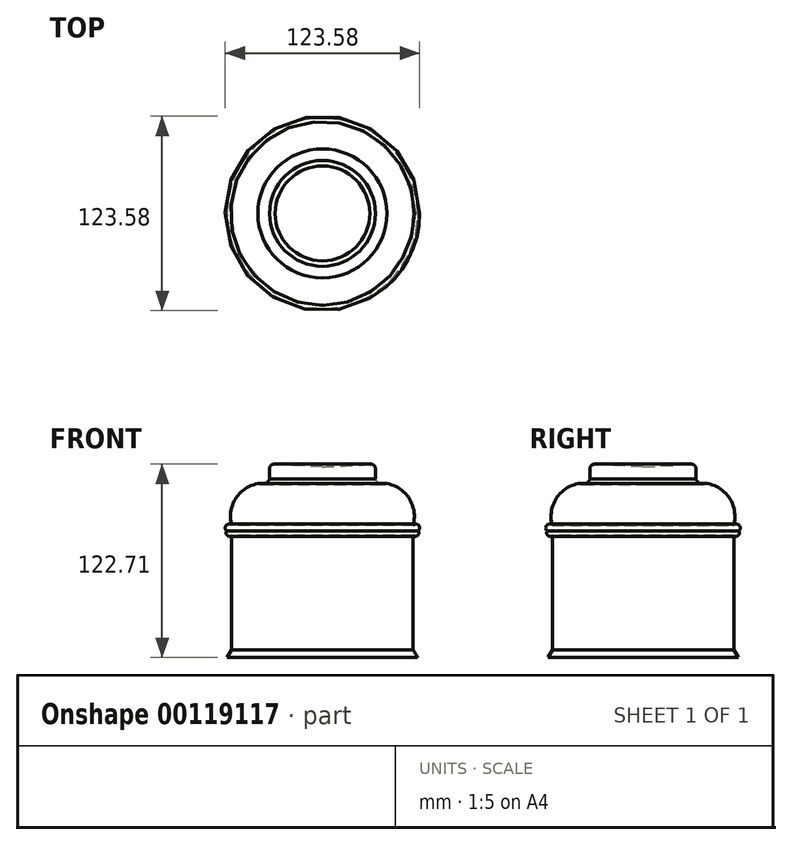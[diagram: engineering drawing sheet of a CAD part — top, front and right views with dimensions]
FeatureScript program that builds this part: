
annotation { "Feature Type Name" : "Feature", "Feature Type Description" : "" }
export const myFeature = defineFeature(function(context is Context, id is Id, definition is map)
    precondition{}
    {
        {
            var Q0;
            Q0=qCreatedBy(makeId("Front.planeOp"),FACE);
            var sketch = newSketch(context, id + "F0", { "sketchPlane" : qUnion([Q0])});
            skLineSegment(sketch, "E0", {"start": v(-30.08, 58.25) * mm, "end": v(-30.08, -62.73) * mm});
            skLineSegment(sketch, "E1", {"start": v(-30.08, -62.73) * mm, "end": v(30.4, -62.73) * mm});
            skLineSegment(sketch, "E2", {"start": v(30.4, -62.73) * mm, "end": v(27.52, -57.93) * mm});
            skLineSegment(sketch, "E3", {"start": v(27.52, -57.93) * mm, "end": v(27.52, 14.72) * mm});
            skArc(sketch, "E4", {"start": v(27.52, 14.72) * mm, "mid": v(31.12, 16.32) * mm, "end": v(27.52, 17.92) * mm});
            skArc(sketch, "E5", {"start": v(27.52, 17.92) * mm, "mid": v(31.7, 19.52) * mm, "end": v(27.52, 21.12) * mm});
            skArc(sketch, "E6", {"start": v(27.52, 21.12) * mm, "mid": v(25.06, 38.07) * mm, "end": v(10.88, 47.68) * mm});
            skArc(sketch, "E7", {"start": v(3.52, 50.56) * mm, "mid": v(6.57, 47.51) * mm, "end": v(10.88, 47.68) * mm});
            skLineSegment(sketch, "E8", {"start": v(3.52, 50.56) * mm, "end": v(3.52, 57.29) * mm});
            skArc(sketch, "E9", {"start": v(3.52, 57.29) * mm, "mid": v(2.41, 59.46) * mm, "end": v(0, 59.85) * mm});
            skLineSegment(sketch, "E10", {"start": v(-30.08, 58.25) * mm, "end": v(0, 59.85) * mm});
            skSolve(sketch);
        }
        {
            var Q0;
            Q0 = qSketchRegion(id + "F0", true);
            var Q1;
            Q1=sQuery(id+"F0.wireOp",EDGE,"E0");
            revolve(context, id + "F1", {"entities" : qUnion([Q0]), "axis" : qUnion([Q1]), "revolveType" : RevolveType.FULL});
        }
    });
